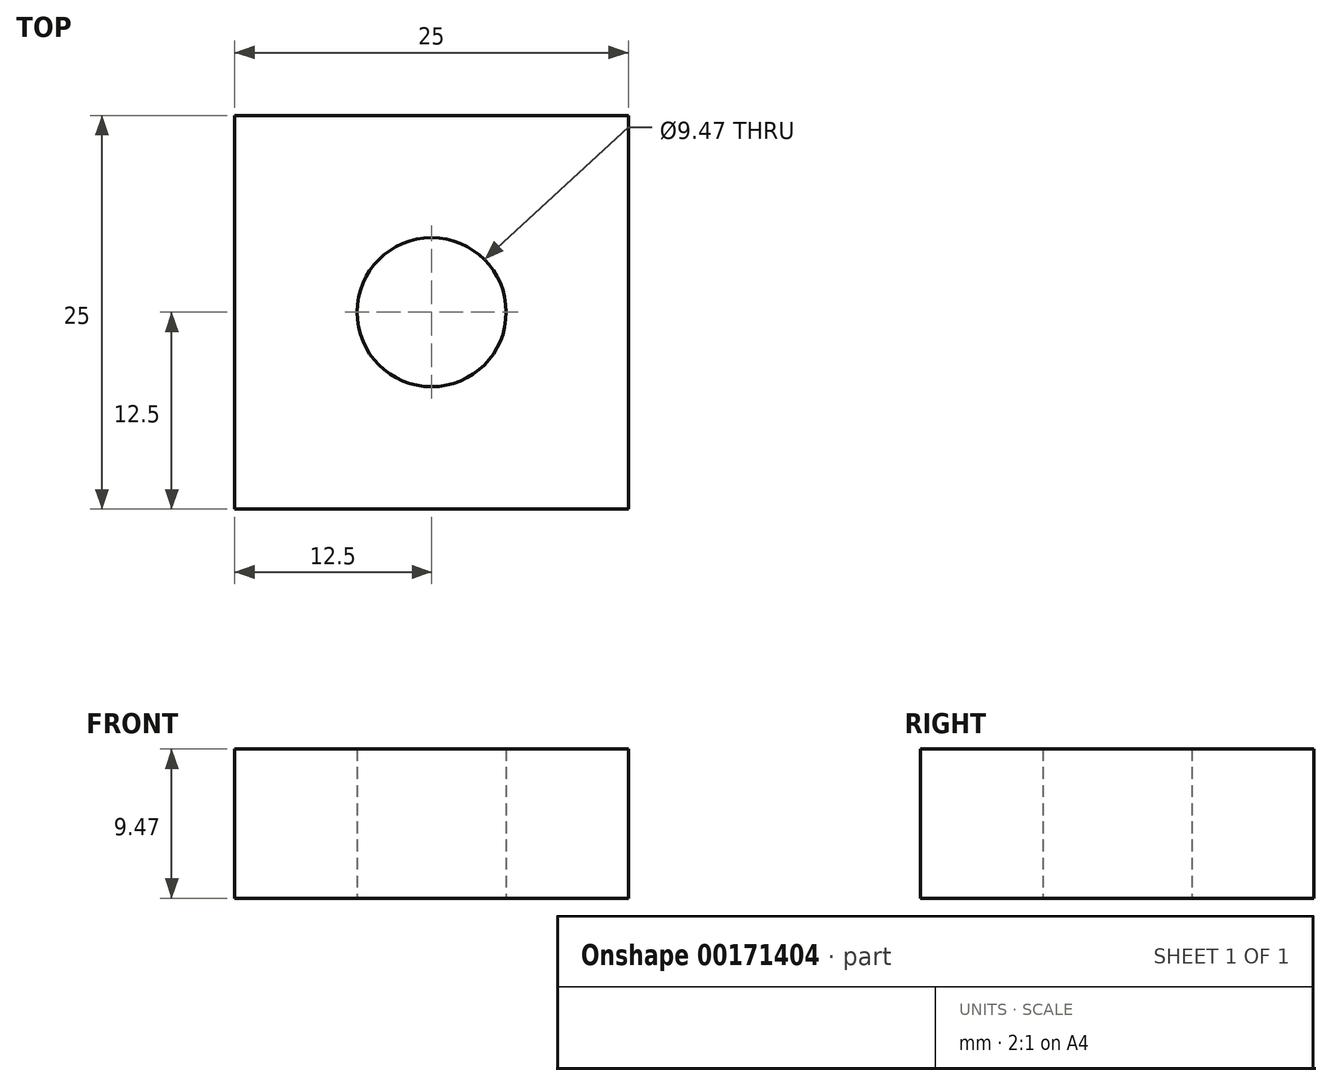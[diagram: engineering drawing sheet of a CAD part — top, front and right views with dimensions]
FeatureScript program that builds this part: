
annotation { "Feature Type Name" : "Feature", "Feature Type Description" : "" }
export const myFeature = defineFeature(function(context is Context, id is Id, definition is map)
    precondition{}
    {
        {
            assignVariable(context, id + "F0", {"name" : "diameter_shaft", "anyValue" : 9.47});
        }
        {
            assignVariable(context, id + "F1", {"name" : "allowance_inner", "anyValue" : 0});
        }
        {
            var Q0;
            Q0=qCreatedBy(makeId("Top.planeOp"),FACE);
            var sketch = newSketch(context, id + "F2", { "sketchPlane" : qUnion([Q0])});
            skLineSegment(sketch, "E0.bottom", {"start": v(12.5, -12.5) * mm, "end": v(-12.5, -12.5) * mm});
            skLineSegment(sketch, "E0.top", {"start": v(12.5, 12.5) * mm, "end": v(-12.5, 12.5) * mm});
            skLineSegment(sketch, "E0.left", {"start": v(12.5, -12.5) * mm, "end": v(12.5, 12.5) * mm});
            skLineSegment(sketch, "E0.right", {"start": v(-12.5, -12.5) * mm, "end": v(-12.5, 12.5) * mm});
            skPoint(sketch, "E0.middle", {"position": v(0, 0) * mm});
            skCircle(sketch, "E1", {"center": v(0, 0) * mm, "radius": 4.74 * mm});
            skSolve(sketch);
        }
        {
            var Q0;
            Q0=makeQuery(id+"F2.imprint","IMPRINT",FACE,{"disambiguationData":[TD([[makeQuery(id+"F2.imprint","IMPRINT",EDGE,{"derivedFrom":sQuery(id+"F2.wireOp",EDGE,"E0.bottom")}),-1.0]])]});
            extrude(context, id + "F3", {"entities" : qUnion([Q0]), "depth" : (getVariable(context, 'diameter_shaft') - getVariable(context, 'allowance_inner')) * mm});
        }
    });
